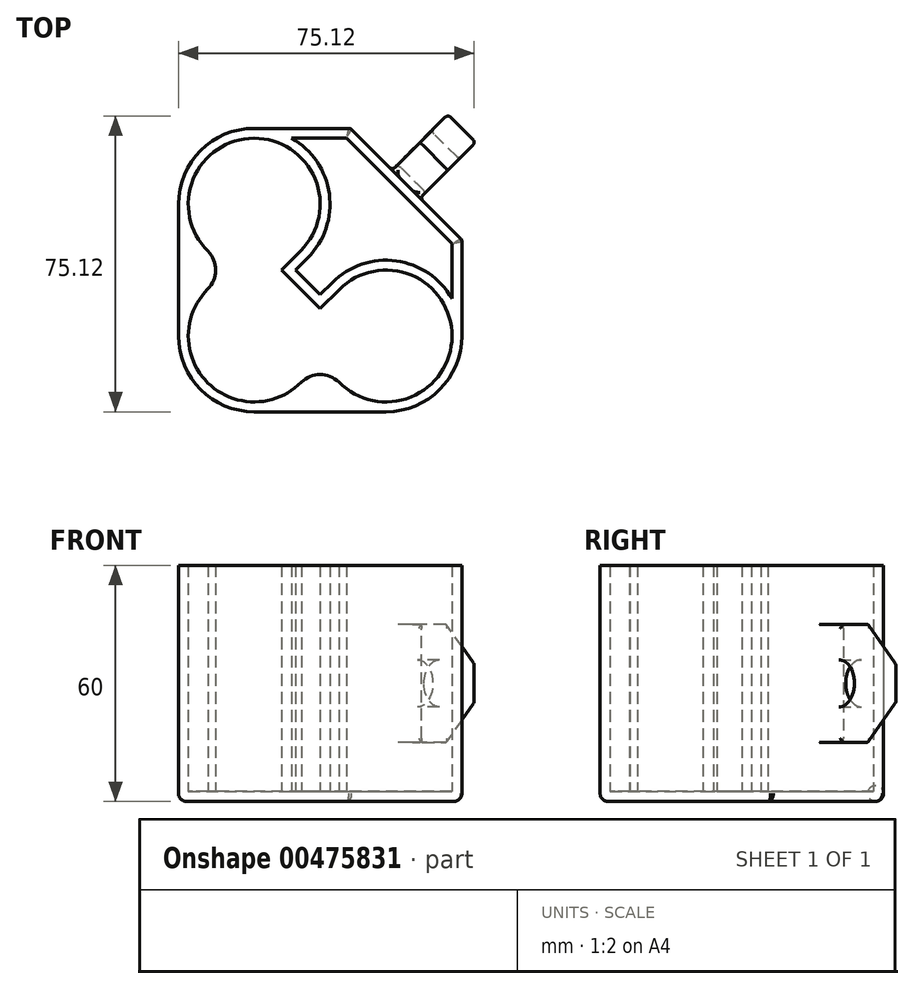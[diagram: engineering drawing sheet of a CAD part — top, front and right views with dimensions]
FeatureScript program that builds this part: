
annotation { "Feature Type Name" : "Feature", "Feature Type Description" : "" }
export const myFeature = defineFeature(function(context is Context, id is Id, definition is map)
    precondition{}
    {
        {
            var Q0;
            Q0=qCreatedBy(makeId("Top.planeOp"),FACE);
            var sketch = newSketch(context, id + "F0", { "sketchPlane" : qUnion([Q0])});
            skLineSegment(sketch, "E0.bottom", {"start": v(16.75, -36) * mm, "end": v(-16.75, -36) * mm});
            skLineSegment(sketch, "E0.top", {"start": v(7.72, 36) * mm, "end": v(-16.75, 36) * mm});
            skLineSegment(sketch, "E0.left", {"start": v(36, -16.75) * mm, "end": v(36, 7.72) * mm});
            skLineSegment(sketch, "E0.right", {"start": v(-36, -16.75) * mm, "end": v(-36, 16.75) * mm});
            skPoint(sketch, "E0.middle", {"position": v(0, 0) * mm});
            skArc(sketch, "E1", {"start": v(4.79, -28.47) * mm, "mid": v(33.5, -16.83) * mm, "end": v(4.9, -4.9) * mm});
            skArc(sketch, "E2", {"start": v(-28.57, -4.88) * mm, "mid": v(-28.55, -28.64) * mm, "end": v(-4.78, -28.47) * mm});
            skArc(sketch, "E3", {"start": v(-4.9, 4.9) * mm, "mid": v(-16.81, 33.5) * mm, "end": v(-28.5, 4.82) * mm});
            skArc(sketch, "E4", {"start": v(-3.14, 3.14) * mm, "mid": v(2.32, 19.34) * mm, "end": v(-7.26, 33.5) * mm});
            skLineSegment(sketch, "E5", {"start": v(36, 36) * mm, "end": v(-36, -36) * mm, "construction": true});
            skLineSegment(sketch, "E6", {"start": v(-36, 36) * mm, "end": v(36, -36) * mm, "construction": true});
            skLineSegment(sketch, "E7", {"start": v(36, 7.72) * mm, "end": v(7.72, 36) * mm});
            skLineSegment(sketch, "E8", {"start": v(36, 7.72) * mm, "end": v(36, 36) * mm, "construction": true});
            skLineSegment(sketch, "E9", {"start": v(36, 36) * mm, "end": v(7.72, 36) * mm, "construction": true});
            skLineSegment(sketch, "E10", {"start": v(3.14, -3.14) * mm, "end": v(0, -6.28) * mm});
            skLineSegment(sketch, "E11", {"start": v(0, -6.28) * mm, "end": v(-6.28, 0) * mm});
            skLineSegment(sketch, "E12", {"start": v(-6.28, 0) * mm, "end": v(-3.14, 3.14) * mm});
            skLineSegment(sketch, "E13.bottom", {"start": v(33.5, -33.5) * mm, "end": v(7.26, -33.5) * mm, "construction": true});
            skLineSegment(sketch, "E13.top", {"start": v(33.5, 33.5) * mm, "end": v(10.22, 33.5) * mm, "construction": true});
            skLineSegment(sketch, "E13.left", {"start": v(33.5, -33.5) * mm, "end": v(33.5, -16.75) * mm, "construction": true});
            skLineSegment(sketch, "E13.right", {"start": v(-33.5, -33.5) * mm, "end": v(-33.5, -7.26) * mm, "construction": true});
            skLineSegment(sketch, "E14", {"start": v(-4.9, 4.9) * mm, "end": v(-9.81, 0) * mm});
            skLineSegment(sketch, "E15", {"start": v(4.9, -4.9) * mm, "end": v(0, -9.81) * mm});
            skLineSegment(sketch, "E16", {"start": v(0, -9.81) * mm, "end": v(-9.81, 0) * mm});
            skArc(sketch, "E17.trimOffspring", {"start": v(16.75, -36) * mm, "mid": v(30.36, -30.36) * mm, "end": v(36, -16.75) * mm});
            skArc(sketch, "E18.trimOffspring", {"start": v(-36, -16.75) * mm, "mid": v(-30.36, -30.36) * mm, "end": v(-16.75, -36) * mm});
            skLineSegment(sketch, "E19", {"start": v(-7.26, 33.5) * mm, "end": v(6.68, 33.5) * mm});
            skLineSegment(sketch, "E20", {"start": v(33.5, -7.26) * mm, "end": v(33.5, 6.68) * mm});
            skArc(sketch, "E21.trimOffspring", {"start": v(33.5, -7.26) * mm, "mid": v(19.34, 2.32) * mm, "end": v(3.14, -3.14) * mm});
            skArc(sketch, "E22.trimOffspring", {"start": v(-16.75, 36) * mm, "mid": v(-30.36, 30.36) * mm, "end": v(-36, 16.75) * mm});
            skLineSegment(sketch, "E23.trimOffspring", {"start": v(-16.75, 33.5) * mm, "end": v(-33.5, 33.5) * mm, "construction": true});
            skLineSegment(sketch, "E24", {"start": v(21.86, 21.86) * mm, "end": v(20.1, 20.1) * mm, "construction": true});
            skLineSegment(sketch, "E25", {"start": v(20.1, 20.1) * mm, "end": v(6.68, 33.5) * mm, "construction": true});
            skLineSegment(sketch, "E26", {"start": v(6.68, 33.5) * mm, "end": v(33.5, 6.68) * mm});
            skLineSegment(sketch, "E27.trimOffspring", {"start": v(33.5, 10.22) * mm, "end": v(33.5, 33.5) * mm, "construction": true});
            skLineSegment(sketch, "E28", {"start": v(36, 15.05) * mm, "end": v(33.5, 15.05) * mm, "construction": true});
            skLineSegment(sketch, "E29.trimOffspring", {"start": v(6.68, 33.5) * mm, "end": v(-7.26, 33.5) * mm, "construction": true});
            skLineSegment(sketch, "E30.trimOffspring", {"start": v(-33.5, 7.26) * mm, "end": v(-33.5, 33.5) * mm, "construction": true});
            skLineSegment(sketch, "E31", {"start": v(-33.5, 7.26) * mm, "end": v(-33.5, -7.26) * mm, "construction": true});
            skLineSegment(sketch, "E32.trimOffspring", {"start": v(-7.26, -33.5) * mm, "end": v(-33.5, -33.5) * mm, "construction": true});
            skLineSegment(sketch, "E33", {"start": v(7.26, -33.5) * mm, "end": v(-7.26, -33.5) * mm, "construction": true});
            skArc(sketch, "E34", {"start": v(-28.57, -4.88) * mm, "mid": v(-26.56, -0.04) * mm, "end": v(-28.5, 4.82) * mm});
            skArc(sketch, "E35", {"start": v(5.02, -28.71) * mm, "mid": v(0.17, -26.56) * mm, "end": v(-4.78, -28.47) * mm});
            skLineSegment(sketch, "E36", {"start": v(-16.75, 16.75) * mm, "end": v(-3.14, 30.36) * mm, "construction": true});
            skLineSegment(sketch, "E37", {"start": v(16.75, -16.75) * mm, "end": v(30.36, -3.14) * mm, "construction": true});
            skLineSegment(sketch, "E38", {"start": v(-3.14, 30.36) * mm, "end": v(30.36, -3.14) * mm, "construction": true});
            skLineSegment(sketch, "E39", {"start": v(30.36, -3.14) * mm, "end": v(32.37, -5.15) * mm, "construction": true});
            skLineSegment(sketch, "E40", {"start": v(-3.14, 30.36) * mm, "end": v(-5.15, 32.37) * mm, "construction": true});
            skLineSegment(sketch, "E41", {"start": v(13.61, 13.61) * mm, "end": v(14.74, 14.74) * mm, "construction": true});
            skLineSegment(sketch, "E42", {"start": v(14.74, 14.74) * mm, "end": v(33.5, -4.01) * mm, "construction": true});
            skLineSegment(sketch, "E43", {"start": v(33.5, -4.01) * mm, "end": v(32.37, -5.15) * mm, "construction": true});
            skLineSegment(sketch, "E44", {"start": v(14.74, 14.74) * mm, "end": v(-4.01, 33.5) * mm, "construction": true});
            skLineSegment(sketch, "E45", {"start": v(-4.01, 33.5) * mm, "end": v(-5.15, 32.37) * mm, "construction": true});
            skSolve(sketch);
        }
        {
            var Q0;
            Q0 = qSketchRegion(id + "F0", true);
            extrude(context, id + "F1", {"entities" : qUnion([Q0]), "depth" : 60 * mm});
        }
        {
            var Q0;
            Q0=makeQuery(id+"F1.opExtrude","SWEPT_FACE",FACE,{"disambiguationData":[OSD([sQuery(id+"F0.wireOp",EDGE,"E7")])]});
            var sketch = newSketch(context, id + "F2", { "sketchPlane" : qUnion([Q0])});
            skLineSegment(sketch, "E46.bottom", {"start": v(-5, 45) * mm, "end": v(5, 45) * mm});
            skLineSegment(sketch, "E46.top", {"start": v(-5, 15) * mm, "end": v(5, 15) * mm});
            skLineSegment(sketch, "E46.left", {"start": v(-5, 45) * mm, "end": v(-5, 15) * mm});
            skLineSegment(sketch, "E46.right", {"start": v(5, 45) * mm, "end": v(5, 15) * mm});
            skPoint(sketch, "E46.middle", {"position": v(0, 30) * mm});
            skLineSegment(sketch, "E47", {"start": v(0, 30) * mm, "end": v(0, 0) * mm, "construction": true});
            skLineSegment(sketch, "E48", {"start": v(0, 30) * mm, "end": v(0, 60) * mm, "construction": true});
            skSolve(sketch);
        }
        {
            var Q0;
            Q0 = qSketchRegion(id + "F2", true);
            extrude(context, id + "F3", {"entities" : qUnion([Q0]), "operationType" : NewBodyOperationType.ADD, "depth" : 20 * mm});
        }
        {
            var Q0;
            Q0=makeQuery(id+"F3.opExtrude","SWEPT_FACE",FACE,{"disambiguationData":[OSD([sQuery(id+"F2.wireOp",EDGE,"E46.right")])]});
            var sketch = newSketch(context, id + "F4", { "sketchPlane" : qUnion([Q0])});
            skCircle(sketch, "E49", {"center": v(-38.91, 30) * mm, "radius": 6 * mm});
            skPoint(sketch, "E49.centerSnap0", {"position": v(-38.91, 40) * mm});
            skPoint(sketch, "E49.centerSnap1", {"position": v(-50.91, 30) * mm});
            skSolve(sketch);
        }
        {
            var Q0;
            Q0 = qSketchRegion(id + "F4", true);
            extrude(context, id + "F5", {"entities" : qUnion([Q0]), "operationType" : NewBodyOperationType.REMOVE, "endBound" : BoundingType.UP_TO_NEXT, "oppositeDirection" : true, "depth" : 25 * mm});
        }
        {
            var Q0;
            Q0=makeQuery(id+"F3.opExtrude","CAP_EDGE",EDGE,{"disambiguationData":[OSD([sQuery(id+"F2.wireOp",EDGE,"E46.top")])],"isStart":false});
            var Q1;
            Q1=makeQuery(id+"F3.opExtrude","CAP_EDGE",EDGE,{"disambiguationData":[OSD([sQuery(id+"F2.wireOp",EDGE,"E46.bottom")])],"isStart":false});
            var Q2;
            Q2=makeQuery(id+"F3.opExtrude","CAP_EDGE",EDGE,{"disambiguationData":[OSD([sQuery(id+"F2.wireOp",EDGE,"E46.bottom")])],"isStart":true});
            var Q3;
            Q3=makeQuery(id+"F3.opExtrude","CAP_EDGE",EDGE,{"disambiguationData":[OSD([sQuery(id+"F2.wireOp",EDGE,"E46.top")])],"isStart":true});
            chamfer(context, id + "F6", {"entities" : qUnion([Q0, Q1, Q2, Q3]), "width" : 10 * mm, "tangentPropagation" : true});
        }
        {
            var Q0;
            Q0=makeQuery(id+"F3.opExtrude","SWEPT_FACE",FACE,{"disambiguationData":[OSD([sQuery(id+"F2.wireOp",EDGE,"E46.right")])]});
            var Q1;
            Q1=makeQuery(id+"F3.opExtrude","SWEPT_FACE",FACE,{"disambiguationData":[OSD([sQuery(id+"F2.wireOp",EDGE,"E46.left")])]});
            var Q2;
            Q2=makeQuery(id+"F1.opExtrude","SWEPT_EDGE",EDGE,{"disambiguationData":[OSD([sQuery(id+"F0.wireOp",EDGE,"E0.left"),sQuery(id+"F0.wireOp",EDGE,"E7")])]});
            var Q3;
            Q3=makeQuery(id+"F1.opExtrude","SWEPT_EDGE",EDGE,{"disambiguationData":[OSD([sQuery(id+"F0.wireOp",EDGE,"E0.top"),sQuery(id+"F0.wireOp",EDGE,"E7")])]});
            var Q4;
            {var subQ0=sQuery(id+"F2.wireOp",EDGE,"E46.top");Q4=makeQuery(id+"F6.opChamfer","BLEND_EDGE",EDGE,{"blendedFrom":[makeQuery(id+"F3.opExtrude","CAP_EDGE",EDGE,{"disambiguationData":[OSD([subQ0])],"isStart":false}),makeQuery(id+"F3.opExtrude","CAP_FACE",FACE,{"disambiguationData":[OSD([sQuery(id+"F2.wireOp",EDGE,"E46.bottom"),subQ0,sQuery(id+"F2.wireOp",EDGE,"E46.left"),sQuery(id+"F2.wireOp",EDGE,"E46.right")])],"isStart":false})],"blendedInto":[makeQuery(id+"F3.opExtrude","CAP_FACE",FACE,{"disambiguationData":[OSD([sQuery(id+"F2.wireOp",EDGE,"E46.bottom"),subQ0,sQuery(id+"F2.wireOp",EDGE,"E46.left"),sQuery(id+"F2.wireOp",EDGE,"E46.right")])],"isStart":false})]});}
            var Q5;
            {var subQ0=sQuery(id+"F2.wireOp",EDGE,"E46.bottom");Q5=makeQuery(id+"F6.opChamfer","BLEND_EDGE",EDGE,{"blendedFrom":[makeQuery(id+"F3.opExtrude","CAP_EDGE",EDGE,{"disambiguationData":[OSD([subQ0])],"isStart":false}),makeQuery(id+"F3.opExtrude","CAP_FACE",FACE,{"disambiguationData":[OSD([subQ0,sQuery(id+"F2.wireOp",EDGE,"E46.top"),sQuery(id+"F2.wireOp",EDGE,"E46.left"),sQuery(id+"F2.wireOp",EDGE,"E46.right")])],"isStart":false})],"blendedInto":[makeQuery(id+"F3.opExtrude","CAP_FACE",FACE,{"disambiguationData":[OSD([subQ0,sQuery(id+"F2.wireOp",EDGE,"E46.top"),sQuery(id+"F2.wireOp",EDGE,"E46.left"),sQuery(id+"F2.wireOp",EDGE,"E46.right")])],"isStart":false})]});}
            fillet(context, id + "F7", {"entities" : qUnion([Q0, Q1, Q2, Q3, Q4, Q5]), "radius" : 1 * mm, "tangentPropagation" : true, "allowEdgeOverflow" : false});
        }
        {
            var Q0;
            Q0=makeQuery(id+"F1.opExtrude","CAP_FACE",FACE,{"disambiguationData":[OSD([sQuery(id+"F0.wireOp",EDGE,"E0.bottom"),sQuery(id+"F0.wireOp",EDGE,"E0.top"),sQuery(id+"F0.wireOp",EDGE,"E0.left"),sQuery(id+"F0.wireOp",EDGE,"E0.right"),sQuery(id+"F0.wireOp",EDGE,"E1"),sQuery(id+"F0.wireOp",EDGE,"E2"),sQuery(id+"F0.wireOp",EDGE,"E3"),sQuery(id+"F0.wireOp",EDGE,"E4"),sQuery(id+"F0.wireOp",EDGE,"E7"),sQuery(id+"F0.wireOp",EDGE,"E10"),sQuery(id+"F0.wireOp",EDGE,"E11"),sQuery(id+"F0.wireOp",EDGE,"E12"),sQuery(id+"F0.wireOp",EDGE,"E14"),sQuery(id+"F0.wireOp",EDGE,"E15"),sQuery(id+"F0.wireOp",EDGE,"E16"),sQuery(id+"F0.wireOp",EDGE,"E17.trimOffspring"),sQuery(id+"F0.wireOp",EDGE,"E18.trimOffspring"),sQuery(id+"F0.wireOp",EDGE,"E19"),sQuery(id+"F0.wireOp",EDGE,"E20"),sQuery(id+"F0.wireOp",EDGE,"E21.trimOffspring"),sQuery(id+"F0.wireOp",EDGE,"E22.trimOffspring"),sQuery(id+"F0.wireOp",EDGE,"E26"),sQuery(id+"F0.wireOp",EDGE,"E34"),sQuery(id+"F0.wireOp",EDGE,"E35")])],"isStart":true});
            var sketch = newSketch(context, id + "F8", { "sketchPlane" : qUnion([Q0])});
            skLineSegment(sketch, "E50.0", {"start": v(16.75, 36) * mm, "end": v(-16.75, 36) * mm});
            skArc(sketch, "E51.0", {"start": v(16.75, 36) * mm, "mid": v(30.36, 30.36) * mm, "end": v(36, 16.75) * mm});
            skLineSegment(sketch, "E52.0", {"start": v(36, 16.75) * mm, "end": v(36, -7.3) * mm});
            skLineSegment(sketch, "E53.0", {"start": v(35.7, -8) * mm, "end": v(8, -35.7) * mm});
            skLineSegment(sketch, "E54.0", {"start": v(7.3, -36) * mm, "end": v(-16.75, -36) * mm});
            skArc(sketch, "E55.0", {"start": v(-16.75, -36) * mm, "mid": v(-30.36, -30.36) * mm, "end": v(-36, -16.75) * mm});
            skLineSegment(sketch, "E56.0", {"start": v(-36, 16.75) * mm, "end": v(-36, -16.75) * mm});
            skArc(sketch, "E57.0", {"start": v(-36, 16.75) * mm, "mid": v(-30.36, 30.36) * mm, "end": v(-16.75, 36) * mm});
            skArc(sketch, "E58.0", {"start": v(35.7, -8) * mm, "mid": v(35.92, -7.68) * mm, "end": v(36, -7.3) * mm});
            skArc(sketch, "E59.0", {"start": v(7.3, -36) * mm, "mid": v(7.68, -35.92) * mm, "end": v(8, -35.7) * mm});
            skSolve(sketch);
        }
        {
            var Q0;
            Q0 = qSketchRegion(id + "F8", true);
            extrude(context, id + "F9", {"entities" : qUnion([Q0]), "operationType" : NewBodyOperationType.ADD, "depth" : -2.5 * mm});
        }
        {
            var Q0;
            Q0=makeQuery(id+"F9.boolean.opBoolean","MERGE",FACE,{"derivedFrom":[makeQuery(id+"F1.opExtrude","CAP_FACE",FACE,{"disambiguationData":[OSD([sQuery(id+"F0.wireOp",EDGE,"E0.bottom"),sQuery(id+"F0.wireOp",EDGE,"E0.top"),sQuery(id+"F0.wireOp",EDGE,"E0.left"),sQuery(id+"F0.wireOp",EDGE,"E0.right"),sQuery(id+"F0.wireOp",EDGE,"E1"),sQuery(id+"F0.wireOp",EDGE,"E2"),sQuery(id+"F0.wireOp",EDGE,"E3"),sQuery(id+"F0.wireOp",EDGE,"E4"),sQuery(id+"F0.wireOp",EDGE,"E7"),sQuery(id+"F0.wireOp",EDGE,"E10"),sQuery(id+"F0.wireOp",EDGE,"E11"),sQuery(id+"F0.wireOp",EDGE,"E12"),sQuery(id+"F0.wireOp",EDGE,"E14"),sQuery(id+"F0.wireOp",EDGE,"E15"),sQuery(id+"F0.wireOp",EDGE,"E16"),sQuery(id+"F0.wireOp",EDGE,"E17.trimOffspring"),sQuery(id+"F0.wireOp",EDGE,"E18.trimOffspring"),sQuery(id+"F0.wireOp",EDGE,"E19"),sQuery(id+"F0.wireOp",EDGE,"E20"),sQuery(id+"F0.wireOp",EDGE,"E21.trimOffspring"),sQuery(id+"F0.wireOp",EDGE,"E22.trimOffspring"),sQuery(id+"F0.wireOp",EDGE,"E26"),sQuery(id+"F0.wireOp",EDGE,"E34"),sQuery(id+"F0.wireOp",EDGE,"E35")])],"isStart":true}),makeQuery(id+"F9.opExtrude","CAP_FACE",FACE,{"disambiguationData":[OSD([sQuery(id+"F8.wireOp",EDGE,"E50.0"),sQuery(id+"F8.wireOp",EDGE,"E51.0"),sQuery(id+"F8.wireOp",EDGE,"E52.0"),sQuery(id+"F8.wireOp",EDGE,"E53.0"),sQuery(id+"F8.wireOp",EDGE,"E54.0"),sQuery(id+"F8.wireOp",EDGE,"E55.0"),sQuery(id+"F8.wireOp",EDGE,"E56.0"),sQuery(id+"F8.wireOp",EDGE,"E57.0"),sQuery(id+"F8.wireOp",EDGE,"E58.0"),sQuery(id+"F8.wireOp",EDGE,"E59.0")])],"isStart":true})]});
            fillet(context, id + "F10", {"entities" : qUnion([Q0]), "radius" : 2 * mm, "tangentPropagation" : true, "allowEdgeOverflow" : false});
        }
    });
